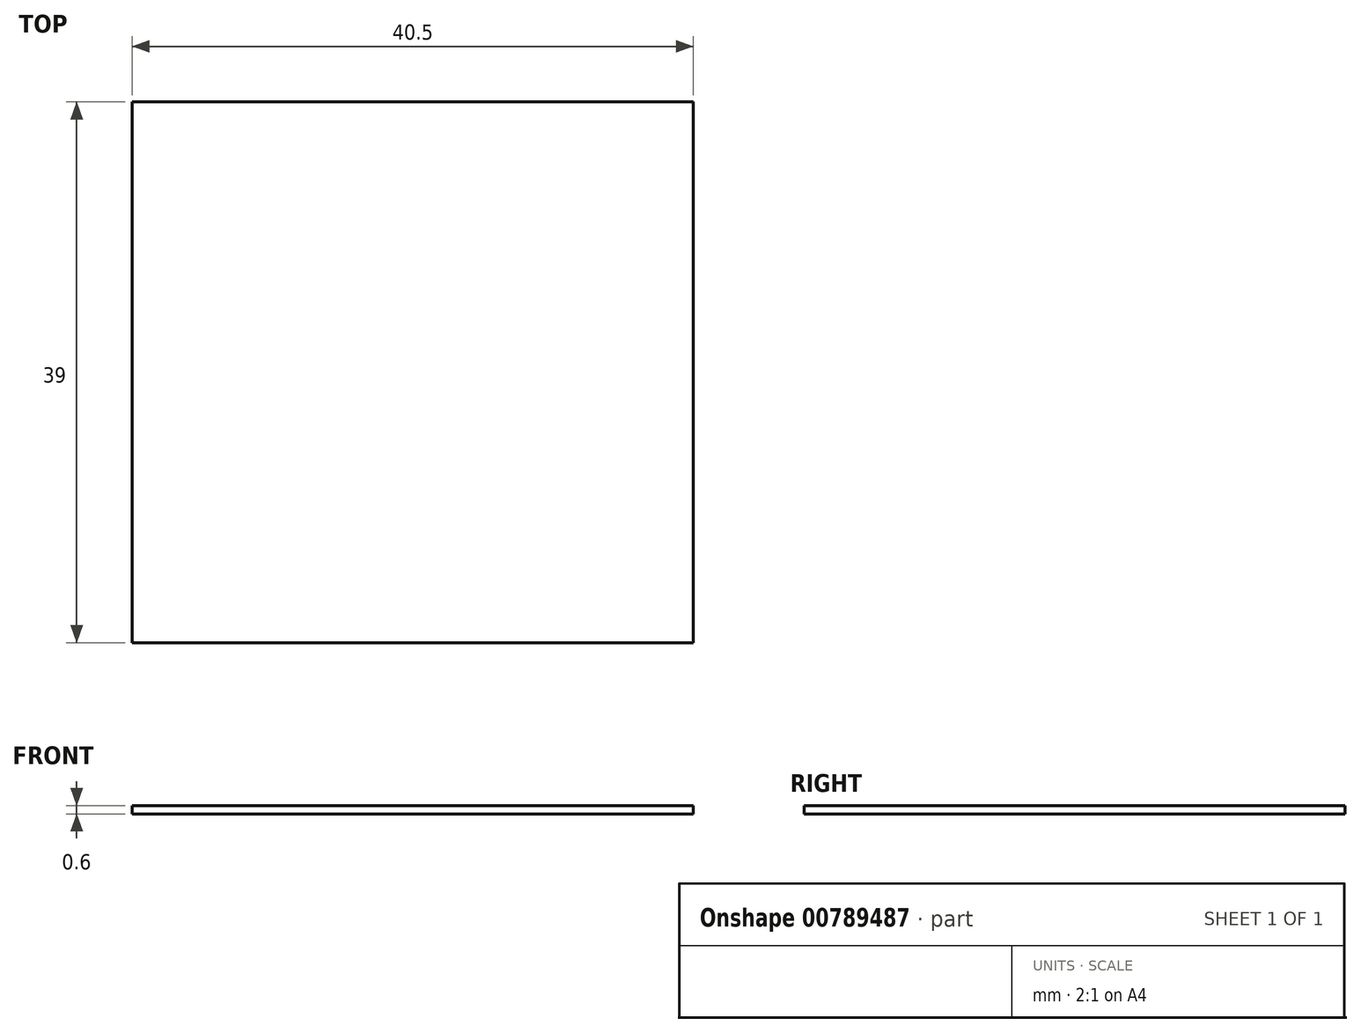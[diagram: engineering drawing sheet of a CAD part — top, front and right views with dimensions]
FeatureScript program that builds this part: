
annotation { "Feature Type Name" : "Feature", "Feature Type Description" : "" }
export const myFeature = defineFeature(function(context is Context, id is Id, definition is map)
    precondition{}
    {
        {
            var Q0;
            Q0=qCreatedBy(makeId("Top.planeOp"),FACE);
            var sketch = newSketch(context, id + "F0", { "sketchPlane" : qUnion([Q0])});
            skLineSegment(sketch, "E0.bottom", {"start": v(0, 0) * mm, "end": v(40.5, 0) * mm});
            skLineSegment(sketch, "E0.top", {"start": v(0, -39) * mm, "end": v(40.5, -39) * mm});
            skLineSegment(sketch, "E0.left", {"start": v(0, 0) * mm, "end": v(0, -39) * mm});
            skLineSegment(sketch, "E0.right", {"start": v(40.5, 0) * mm, "end": v(40.5, -39) * mm});
            skSolve(sketch);
        }
        {
            var Q0;
            Q0=makeQuery(id+"F0.imprint","IMPRINT",FACE,{"disambiguationData":[TD([[makeQuery(id+"F0.imprint","IMPRINT",EDGE,{"derivedFrom":sQuery(id+"F0.wireOp",EDGE,"E0.bottom")}),-1.0]])]});
            extrude(context, id + "F1", {"entities" : qUnion([Q0]), "depth" : 0.6 * mm, "offsetDistance" : 25 * mm});
        }
    });
